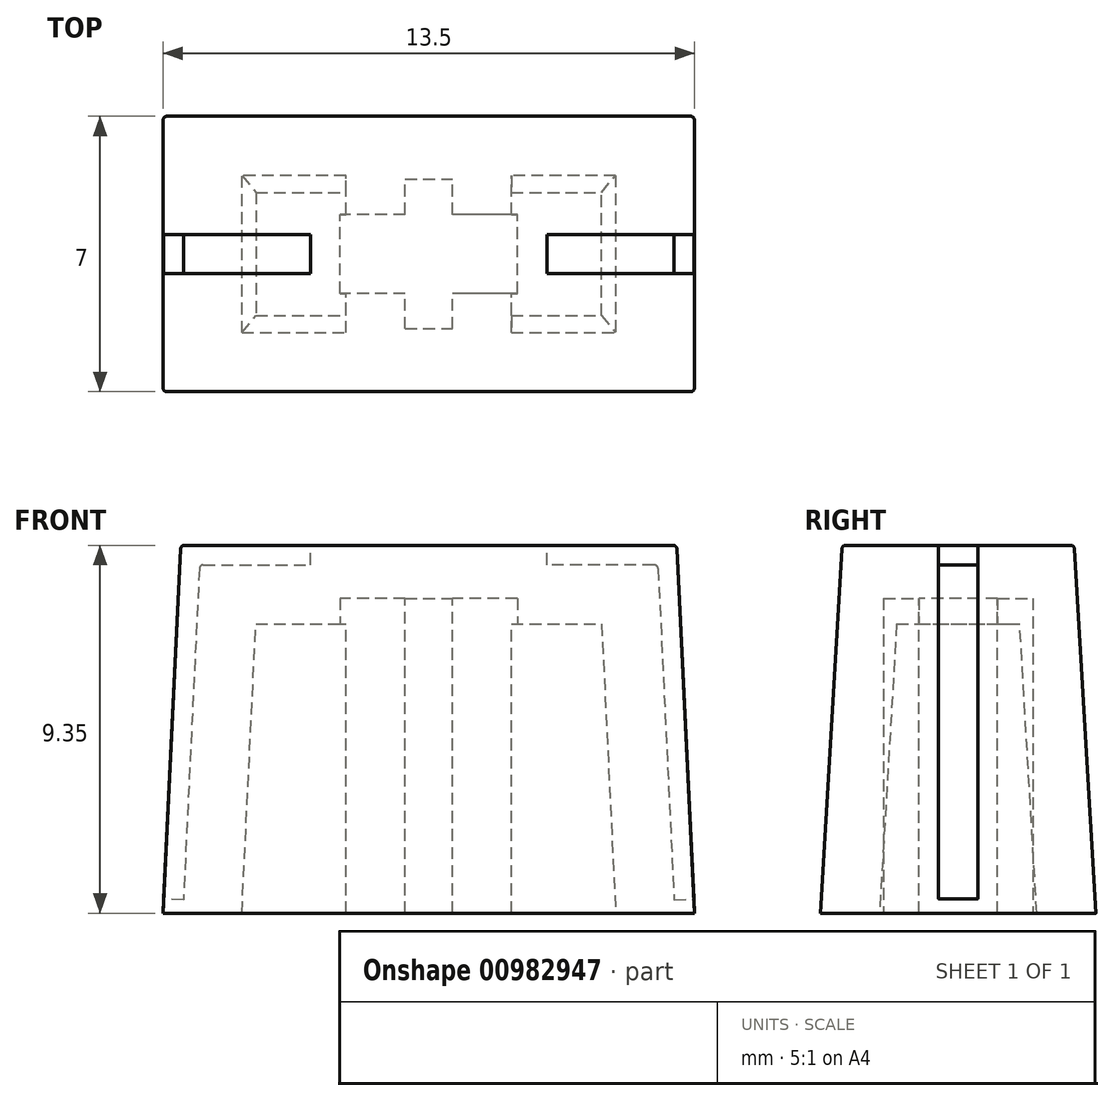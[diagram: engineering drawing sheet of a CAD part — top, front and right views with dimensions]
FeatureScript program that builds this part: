
annotation { "Feature Type Name" : "Feature", "Feature Type Description" : "" }
export const myFeature = defineFeature(function(context is Context, id is Id, definition is map)
    precondition{}
    {
        {
            var Q0;
            Q0=qCreatedBy(makeId("Top.planeOp"),FACE);
            var sketch = newSketch(context, id + "F0", { "sketchPlane" : qUnion([Q0])});
            skLineSegment(sketch, "E0.bottom", {"start": v(6.75, 3.5) * mm, "end": v(-6.75, 3.5) * mm});
            skLineSegment(sketch, "E0.top", {"start": v(6.75, -3.5) * mm, "end": v(-6.75, -3.5) * mm});
            skLineSegment(sketch, "E0.left", {"start": v(6.75, 3.5) * mm, "end": v(6.75, -3.5) * mm});
            skLineSegment(sketch, "E0.right", {"start": v(-6.75, 3.5) * mm, "end": v(-6.75, -3.5) * mm});
            skPoint(sketch, "E0.middle", {"position": v(0, 0) * mm});
            skSolve(sketch);
        }
        {
            var Q0;
            Q0=makeQuery(id+"F0.imprint","IMPRINT",FACE,{"disambiguationData":[TD([[makeQuery(id+"F0.imprint","IMPRINT",EDGE,{"derivedFrom":sQuery(id+"F0.wireOp",EDGE,"E0.bottom")}),1.0]])]});
            extrude(context, id + "F1", {"entities" : qUnion([Q0]), "depth" : 9.35 * mm, "offsetDistance" : 25 * mm});
        }
        {
            var Q0;
            Q0=makeQuery(id+"F1.opExtrude","CAP_EDGE",EDGE,{"disambiguationData":[OSD([sQuery(id+"F0.wireOp",EDGE,"E0.top")])],"isStart":false});
            var Q1;
            Q1=makeQuery(id+"F1.opExtrude","CAP_EDGE",EDGE,{"disambiguationData":[OSD([sQuery(id+"F0.wireOp",EDGE,"E0.bottom")])],"isStart":false});
            chamfer(context, id + "F2", {"entities" : qUnion([Q0, Q1]), "chamferType" : ChamferType.OFFSET_ANGLE, "width" : 9.35 * mm, "oppositeDirection" : false, "angle" : 3.37 * degree, "tangentPropagation" : true});
        }
        {
            var Q0;
            Q0=makeQuery(id+"F1.opExtrude","CAP_EDGE",EDGE,{"disambiguationData":[OSD([sQuery(id+"F0.wireOp",EDGE,"E0.right")])],"isStart":false});
            var Q1;
            Q1=makeQuery(id+"F1.opExtrude","CAP_EDGE",EDGE,{"disambiguationData":[OSD([sQuery(id+"F0.wireOp",EDGE,"E0.left")])],"isStart":false});
            chamfer(context, id + "F3", {"entities" : qUnion([Q0, Q1]), "chamferType" : ChamferType.OFFSET_ANGLE, "width" : 9.35 * mm, "oppositeDirection" : true, "angle" : 2.76 * degree, "tangentPropagation" : true});
        }
        {
            var Q0;
            Q0=makeQuery(id+"F1.opExtrude","CAP_FACE",FACE,{"disambiguationData":[OSD([sQuery(id+"F0.wireOp",EDGE,"E0.bottom"),sQuery(id+"F0.wireOp",EDGE,"E0.top"),sQuery(id+"F0.wireOp",EDGE,"E0.left"),sQuery(id+"F0.wireOp",EDGE,"E0.right")])],"isStart":true});
            var sketch = newSketch(context, id + "F4", { "sketchPlane" : qUnion([Q0])});
            skLineSegment(sketch, "E1.bottom", {"start": v(-0.6, 1.9) * mm, "end": v(0.6, 1.9) * mm});
            skLineSegment(sketch, "E1.top", {"start": v(-0.6, -1.9) * mm, "end": v(0.6, -1.9) * mm});
            skLineSegment(sketch, "E1.left", {"start": v(-0.6, 1.9) * mm, "end": v(-0.6, -1.9) * mm});
            skLineSegment(sketch, "E1.right", {"start": v(0.6, 1.9) * mm, "end": v(0.6, -1.9) * mm});
            skPoint(sketch, "E1.middle", {"position": v(0, 0) * mm});
            skSolve(sketch);
        }
        {
            var Q0;
            Q0=makeQuery(id+"F4.imprint","IMPRINT",FACE,{"disambiguationData":[TD([[makeQuery(id+"F4.imprint","IMPRINT",EDGE,{"derivedFrom":sQuery(id+"F4.wireOp",EDGE,"E1.bottom")}),-1.0]])]});
            extrude(context, id + "F5", {"entities" : qUnion([Q0]), "operationType" : NewBodyOperationType.REMOVE, "oppositeDirection" : true, "depth" : 8 * mm, "offsetDistance" : 25 * mm});
        }
        {
            var Q0;
            Q0=makeQuery(id+"F1.opExtrude","CAP_FACE",FACE,{"disambiguationData":[OSD([sQuery(id+"F0.wireOp",EDGE,"E0.bottom"),sQuery(id+"F0.wireOp",EDGE,"E0.top"),sQuery(id+"F0.wireOp",EDGE,"E0.left"),sQuery(id+"F0.wireOp",EDGE,"E0.right")])],"isStart":false});
            var sketch = newSketch(context, id + "F6", { "sketchPlane" : qUnion([Q0])});
            skLineSegment(sketch, "E2.bottom", {"start": v(-6.3, -0.5) * mm, "end": v(-3, -0.5) * mm});
            skLineSegment(sketch, "E2.top", {"start": v(-6.3, 0.5) * mm, "end": v(-3, 0.5) * mm});
            skLineSegment(sketch, "E2.left", {"start": v(-6.3, -0.5) * mm, "end": v(-6.3, 0.5) * mm});
            skLineSegment(sketch, "E2.right", {"start": v(-3, -0.5) * mm, "end": v(-3, 0.5) * mm});
            skLineSegment(sketch, "E3.MirrorCS", {"start": v(6.3, 0.5) * mm, "end": v(3, 0.5) * mm});
            skLineSegment(sketch, "E4.MirrorCS", {"start": v(6.3, -0.5) * mm, "end": v(3, -0.5) * mm});
            skLineSegment(sketch, "E5.MirrorCS", {"start": v(3, -0.5) * mm, "end": v(3, 0.5) * mm});
            skLineSegment(sketch, "E6.MirrorCS", {"start": v(6.3, -0.5) * mm, "end": v(6.3, 0.5) * mm});
            skSolve(sketch);
        }
        {
            var Q0;
            Q0=makeQuery(id+"F6.imprint","IMPRINT",FACE,{"disambiguationData":[TD([[makeQuery(id+"F6.imprint","IMPRINT",EDGE,{"derivedFrom":sQuery(id+"F6.wireOp",EDGE,"E2.bottom")}),1.0]])]});
            var Q1;
            Q1=makeQuery(id+"F6.imprint","IMPRINT",FACE,{"disambiguationData":[TD([[makeQuery(id+"F6.imprint","IMPRINT",EDGE,{"derivedFrom":sQuery(id+"F6.wireOp",EDGE,"E3.MirrorCS")}),1.0]])]});
            extrude(context, id + "F7", {"entities" : qUnion([Q0, Q1]), "operationType" : NewBodyOperationType.REMOVE, "oppositeDirection" : true, "depth" : 0.5 * mm, "offsetDistance" : 25 * mm});
        }
        {
            var Q0;
            Q0=makeQuery(id+"F3.opChamfer","BLEND_FACE",FACE,{"disambiguationData":[OSD([sQuery(id+"F0.wireOp",EDGE,"E0.right")])]});
            var sketch = newSketch(context, id + "F8", { "sketchPlane" : qUnion([Q0])});
            skLineSegment(sketch, "E7.bottom", {"start": v(-0.5, 9.04) * mm, "end": v(0.5, 9.04) * mm});
            skLineSegment(sketch, "E7.top", {"start": v(-0.5, 0.04) * mm, "end": v(0.5, 0.04) * mm});
            skLineSegment(sketch, "E7.left", {"start": v(-0.5, 9.04) * mm, "end": v(-0.5, 0.04) * mm});
            skLineSegment(sketch, "E7.right", {"start": v(0.5, 9.04) * mm, "end": v(0.5, 0.04) * mm});
            skSolve(sketch);
        }
        {
            var Q0;
            Q0=makeQuery(id+"F8.imprint","IMPRINT",FACE,{"disambiguationData":[TD([[makeQuery(id+"F8.imprint","IMPRINT",EDGE,{"derivedFrom":sQuery(id+"F8.wireOp",EDGE,"E7.bottom")}),-1.0]])]});
            extrude(context, id + "F9", {"entities" : qUnion([Q0]), "operationType" : NewBodyOperationType.REMOVE, "oppositeDirection" : true, "depth" : 0.5 * mm, "offsetDistance" : 25 * mm});
        }
        {
            var Q0;
            Q0=makeQuery(id+"F3.opChamfer","BLEND_FACE",FACE,{"disambiguationData":[OSD([sQuery(id+"F0.wireOp",EDGE,"E0.left")])]});
            var sketch = newSketch(context, id + "F10", { "sketchPlane" : qUnion([Q0])});
            skLineSegment(sketch, "E8.bottom", {"start": v(-0.5, 9.04) * mm, "end": v(0.5, 9.04) * mm});
            skLineSegment(sketch, "E8.top", {"start": v(-0.5, 0.04) * mm, "end": v(0.5, 0.04) * mm});
            skLineSegment(sketch, "E8.left", {"start": v(-0.5, 9.04) * mm, "end": v(-0.5, 0.04) * mm});
            skLineSegment(sketch, "E8.right", {"start": v(0.5, 9.04) * mm, "end": v(0.5, 0.04) * mm});
            skSolve(sketch);
        }
        {
            var Q0;
            Q0=makeQuery(id+"F10.imprint","IMPRINT",FACE,{"disambiguationData":[TD([[makeQuery(id+"F10.imprint","IMPRINT",EDGE,{"derivedFrom":sQuery(id+"F10.wireOp",EDGE,"E8.top")}),1.0]])]});
            extrude(context, id + "F11", {"entities" : qUnion([Q0]), "operationType" : NewBodyOperationType.REMOVE, "oppositeDirection" : true, "depth" : 0.5 * mm, "offsetDistance" : 25 * mm});
        }
        {
            var Q0;
            Q0=makeQuery(id+"F1.opExtrude","CAP_FACE",FACE,{"disambiguationData":[OSD([sQuery(id+"F0.wireOp",EDGE,"E0.bottom"),sQuery(id+"F0.wireOp",EDGE,"E0.top"),sQuery(id+"F0.wireOp",EDGE,"E0.left"),sQuery(id+"F0.wireOp",EDGE,"E0.right")])],"isStart":true});
            shell(context, id + "F12", {"entities" : qUnion([Q0]), "thickness" : 1.5 * mm});
        }
        {
            var Q0;
            Q0=makeQuery(id+"F1.opExtrude","CAP_FACE",FACE,{"disambiguationData":[OSD([sQuery(id+"F0.wireOp",EDGE,"E0.bottom"),sQuery(id+"F0.wireOp",EDGE,"E0.top"),sQuery(id+"F0.wireOp",EDGE,"E0.left"),sQuery(id+"F0.wireOp",EDGE,"E0.right")])],"isStart":true});
            var sketch = newSketch(context, id + "F13", { "sketchPlane" : qUnion([Q0])});
            skLineSegment(sketch, "E9.bottom", {"start": v(2.25, -1) * mm, "end": v(-2.25, -1) * mm});
            skLineSegment(sketch, "E9.top", {"start": v(2.25, 1) * mm, "end": v(-2.25, 1) * mm});
            skLineSegment(sketch, "E9.left", {"start": v(2.25, -1) * mm, "end": v(2.25, 1) * mm});
            skLineSegment(sketch, "E9.right", {"start": v(-2.25, -1) * mm, "end": v(-2.25, 1) * mm});
            skPoint(sketch, "E9.middle", {"position": v(0, 0) * mm});
            skSolve(sketch);
        }
        {
            var Q0;
            {var subQ0=sQuery(id+"F13.wireOp",EDGE,"E9.bottom");var subQ1=sQuery(id+"F4.wireOp",EDGE,"E1.left");var subQ2=makeQuery(id+"F5.boolean.opBoolean","COPY",EDGE,{"derivedFrom":makeQuery(id+"F5.opExtrude","CAP_EDGE",EDGE,{"disambiguationData":[OSD([subQ1])],"isStart":true})});var subQ3=makeQuery(id+"F13.imprint","INTERSECT",VERTEX,{"derivedFrom":[subQ2,subQ0]});Q0=makeQuery(id+"F13.imprint","IMPRINT",FACE,{"disambiguationData":[TD([[makeQuery(id+"F13.imprint","IMPRINT",EDGE,{"disambiguationData":[TD([[subQ3,-1.0]])],"derivedFrom":subQ0}),-1.0]])]});}
            var Q1;
            {var subQ0=sQuery(id+"F13.wireOp",EDGE,"E9.bottom");var subQ1=sQuery(id+"F4.wireOp",EDGE,"E1.right");var subQ2=makeQuery(id+"F12.opShell","OFFSET_EDGE",EDGE,{"disambiguationData":[OSD([subQ1])]});var subQ3=makeQuery(id+"F13.imprint","INTERSECT",VERTEX,{"derivedFrom":[subQ2,subQ0]});Q1=makeQuery(id+"F13.imprint","IMPRINT",FACE,{"disambiguationData":[TD([[makeQuery(id+"F13.imprint","IMPRINT",EDGE,{"disambiguationData":[TD([[subQ3,-1.0]])],"derivedFrom":subQ0}),-1.0]])]});}
            extrude(context, id + "F14", {"entities" : qUnion([Q0, Q1]), "operationType" : NewBodyOperationType.REMOVE, "oppositeDirection" : true, "depth" : 8 * mm, "offsetDistance" : 25 * mm});
        }
        {
            var Q0;
            Q0=makeQuery(id+"F3.opChamfer","BLEND_EDGE",EDGE,{"blendedFrom":[makeQuery(id+"F1.opExtrude","CAP_EDGE",EDGE,{"disambiguationData":[OSD([sQuery(id+"F0.wireOp",EDGE,"E0.left")])],"isStart":false}),makeQuery(id+"F2.opChamfer","BLEND_FACE",FACE,{"disambiguationData":[OSD([sQuery(id+"F0.wireOp",EDGE,"E0.top")])]})],"blendedInto":[makeQuery(id+"F2.opChamfer","BLEND_FACE",FACE,{"disambiguationData":[OSD([sQuery(id+"F0.wireOp",EDGE,"E0.top")])]})]});
            var Q1;
            Q1=makeQuery(id+"F3.opChamfer","BLEND_EDGE",EDGE,{"blendedFrom":[makeQuery(id+"F1.opExtrude","CAP_EDGE",EDGE,{"disambiguationData":[OSD([sQuery(id+"F0.wireOp",EDGE,"E0.left")])],"isStart":false}),makeQuery(id+"F2.opChamfer","BLEND_FACE",FACE,{"disambiguationData":[OSD([sQuery(id+"F0.wireOp",EDGE,"E0.bottom")])]})],"blendedInto":[makeQuery(id+"F2.opChamfer","BLEND_FACE",FACE,{"disambiguationData":[OSD([sQuery(id+"F0.wireOp",EDGE,"E0.bottom")])]})]});
            var Q2;
            {var subQ0=sQuery(id+"F0.wireOp",EDGE,"E0.bottom");var subQ1=sQuery(id+"F0.wireOp",EDGE,"E0.left");var subQ2=makeQuery(id+"F1.opExtrude","CAP_FACE",FACE,{"disambiguationData":[OSD([subQ0,sQuery(id+"F0.wireOp",EDGE,"E0.top"),subQ1,sQuery(id+"F0.wireOp",EDGE,"E0.right")])],"isStart":false});Q2=makeQuery(id+"F7.boolean.opBoolean","SPLIT",EDGE,{"disambiguationData":[TD([makeQuery(id+"F2.opChamfer","BLEND_FACE",FACE,{"disambiguationData":[OSD([subQ0])]})])],"derivedFrom":makeQuery(id+"F3.opChamfer","BLEND_EDGE",EDGE,{"blendedFrom":[makeQuery(id+"F1.opExtrude","CAP_EDGE",EDGE,{"disambiguationData":[OSD([subQ1])],"isStart":false}),subQ2],"blendedInto":[subQ2]})});}
            var Q3;
            {var subQ0=sQuery(id+"F0.wireOp",EDGE,"E0.left");var subQ1=sQuery(id+"F0.wireOp",EDGE,"E0.top");var subQ2=makeQuery(id+"F1.opExtrude","CAP_FACE",FACE,{"disambiguationData":[OSD([sQuery(id+"F0.wireOp",EDGE,"E0.bottom"),subQ1,subQ0,sQuery(id+"F0.wireOp",EDGE,"E0.right")])],"isStart":false});Q3=makeQuery(id+"F7.boolean.opBoolean","SPLIT",EDGE,{"disambiguationData":[TD([makeQuery(id+"F2.opChamfer","BLEND_FACE",FACE,{"disambiguationData":[OSD([subQ1])]})])],"derivedFrom":makeQuery(id+"F3.opChamfer","BLEND_EDGE",EDGE,{"blendedFrom":[makeQuery(id+"F1.opExtrude","CAP_EDGE",EDGE,{"disambiguationData":[OSD([subQ0])],"isStart":false}),subQ2],"blendedInto":[subQ2]})});}
            var Q4;
            {var subQ0=sQuery(id+"F0.wireOp",EDGE,"E0.top");Q4=makeQuery(id+"F2.opChamfer","BLEND_EDGE",EDGE,{"blendedFrom":[makeQuery(id+"F1.opExtrude","CAP_EDGE",EDGE,{"disambiguationData":[OSD([subQ0])],"isStart":false}),makeQuery(id+"F1.opExtrude","CAP_FACE",FACE,{"disambiguationData":[OSD([sQuery(id+"F0.wireOp",EDGE,"E0.bottom"),subQ0,sQuery(id+"F0.wireOp",EDGE,"E0.left"),sQuery(id+"F0.wireOp",EDGE,"E0.right")])],"isStart":false})],"blendedInto":[makeQuery(id+"F1.opExtrude","CAP_FACE",FACE,{"disambiguationData":[OSD([sQuery(id+"F0.wireOp",EDGE,"E0.bottom"),subQ0,sQuery(id+"F0.wireOp",EDGE,"E0.left"),sQuery(id+"F0.wireOp",EDGE,"E0.right")])],"isStart":false})]});}
            var Q5;
            {var subQ0=sQuery(id+"F0.wireOp",EDGE,"E0.bottom");Q5=makeQuery(id+"F2.opChamfer","BLEND_EDGE",EDGE,{"blendedFrom":[makeQuery(id+"F1.opExtrude","CAP_EDGE",EDGE,{"disambiguationData":[OSD([subQ0])],"isStart":false}),makeQuery(id+"F1.opExtrude","CAP_FACE",FACE,{"disambiguationData":[OSD([subQ0,sQuery(id+"F0.wireOp",EDGE,"E0.top"),sQuery(id+"F0.wireOp",EDGE,"E0.left"),sQuery(id+"F0.wireOp",EDGE,"E0.right")])],"isStart":false})],"blendedInto":[makeQuery(id+"F1.opExtrude","CAP_FACE",FACE,{"disambiguationData":[OSD([subQ0,sQuery(id+"F0.wireOp",EDGE,"E0.top"),sQuery(id+"F0.wireOp",EDGE,"E0.left"),sQuery(id+"F0.wireOp",EDGE,"E0.right")])],"isStart":false})]});}
            var Q6;
            Q6=makeQuery(id+"F3.opChamfer","BLEND_EDGE",EDGE,{"blendedFrom":[makeQuery(id+"F1.opExtrude","CAP_EDGE",EDGE,{"disambiguationData":[OSD([sQuery(id+"F0.wireOp",EDGE,"E0.right")])],"isStart":false}),makeQuery(id+"F2.opChamfer","BLEND_FACE",FACE,{"disambiguationData":[OSD([sQuery(id+"F0.wireOp",EDGE,"E0.bottom")])]})],"blendedInto":[makeQuery(id+"F2.opChamfer","BLEND_FACE",FACE,{"disambiguationData":[OSD([sQuery(id+"F0.wireOp",EDGE,"E0.bottom")])]})]});
            var Q7;
            Q7=makeQuery(id+"F3.opChamfer","BLEND_EDGE",EDGE,{"blendedFrom":[makeQuery(id+"F1.opExtrude","CAP_EDGE",EDGE,{"disambiguationData":[OSD([sQuery(id+"F0.wireOp",EDGE,"E0.right")])],"isStart":false}),makeQuery(id+"F2.opChamfer","BLEND_FACE",FACE,{"disambiguationData":[OSD([sQuery(id+"F0.wireOp",EDGE,"E0.top")])]})],"blendedInto":[makeQuery(id+"F2.opChamfer","BLEND_FACE",FACE,{"disambiguationData":[OSD([sQuery(id+"F0.wireOp",EDGE,"E0.top")])]})]});
            var Q8;
            {var subQ0=sQuery(id+"F0.wireOp",EDGE,"E0.right");var subQ1=sQuery(id+"F0.wireOp",EDGE,"E0.top");var subQ2=makeQuery(id+"F1.opExtrude","CAP_FACE",FACE,{"disambiguationData":[OSD([sQuery(id+"F0.wireOp",EDGE,"E0.bottom"),subQ1,sQuery(id+"F0.wireOp",EDGE,"E0.left"),subQ0])],"isStart":false});Q8=makeQuery(id+"F7.boolean.opBoolean","SPLIT",EDGE,{"disambiguationData":[TD([makeQuery(id+"F2.opChamfer","BLEND_FACE",FACE,{"disambiguationData":[OSD([subQ1])]})])],"derivedFrom":makeQuery(id+"F3.opChamfer","BLEND_EDGE",EDGE,{"blendedFrom":[makeQuery(id+"F1.opExtrude","CAP_EDGE",EDGE,{"disambiguationData":[OSD([subQ0])],"isStart":false}),subQ2],"blendedInto":[subQ2]})});}
            var Q9;
            {var subQ0=sQuery(id+"F0.wireOp",EDGE,"E0.right");var subQ1=sQuery(id+"F0.wireOp",EDGE,"E0.bottom");var subQ2=makeQuery(id+"F1.opExtrude","CAP_FACE",FACE,{"disambiguationData":[OSD([subQ1,sQuery(id+"F0.wireOp",EDGE,"E0.top"),sQuery(id+"F0.wireOp",EDGE,"E0.left"),subQ0])],"isStart":false});Q9=makeQuery(id+"F7.boolean.opBoolean","SPLIT",EDGE,{"disambiguationData":[TD([makeQuery(id+"F2.opChamfer","BLEND_FACE",FACE,{"disambiguationData":[OSD([subQ1])]})])],"derivedFrom":makeQuery(id+"F3.opChamfer","BLEND_EDGE",EDGE,{"blendedFrom":[makeQuery(id+"F1.opExtrude","CAP_EDGE",EDGE,{"disambiguationData":[OSD([subQ0])],"isStart":false}),subQ2],"blendedInto":[subQ2]})});}
            var Q10;
            Q10=makeQuery(id+"F9.boolean.opBoolean","INTERSECT",EDGE,{"derivedFrom":[makeQuery(id+"F7.boolean.opBoolean","COPY",FACE,{"derivedFrom":makeQuery(id+"F7.opExtrude","CAP_FACE",FACE,{"disambiguationData":[OSD([sQuery(id+"F6.wireOp",EDGE,"E2.bottom"),sQuery(id+"F6.wireOp",EDGE,"E2.top"),sQuery(id+"F6.wireOp",EDGE,"E2.left"),sQuery(id+"F6.wireOp",EDGE,"E2.right")])],"isStart":false})}),makeQuery(id+"F9.opExtrude","CAP_FACE",FACE,{"disambiguationData":[OSD([sQuery(id+"F8.wireOp",EDGE,"E7.bottom"),sQuery(id+"F8.wireOp",EDGE,"E7.top"),sQuery(id+"F8.wireOp",EDGE,"E7.left"),sQuery(id+"F8.wireOp",EDGE,"E7.right")])],"isStart":false})]});
            var Q11;
            Q11=makeQuery(id+"F11.boolean.opBoolean","INTERSECT",EDGE,{"derivedFrom":[makeQuery(id+"F7.boolean.opBoolean","COPY",FACE,{"derivedFrom":makeQuery(id+"F7.opExtrude","CAP_FACE",FACE,{"disambiguationData":[OSD([sQuery(id+"F6.wireOp",EDGE,"E3.MirrorCS"),sQuery(id+"F6.wireOp",EDGE,"E4.MirrorCS"),sQuery(id+"F6.wireOp",EDGE,"E5.MirrorCS"),sQuery(id+"F6.wireOp",EDGE,"E6.MirrorCS")])],"isStart":false})}),makeQuery(id+"F11.opExtrude","CAP_FACE",FACE,{"disambiguationData":[OSD([sQuery(id+"F10.wireOp",EDGE,"E8.bottom"),sQuery(id+"F10.wireOp",EDGE,"E8.top"),sQuery(id+"F10.wireOp",EDGE,"E8.left"),sQuery(id+"F10.wireOp",EDGE,"E8.right")])],"isStart":false})]});
            fillet(context, id + "F15", {"entities" : qUnion([Q0, Q1, Q2, Q3, Q4, Q5, Q6, Q7, Q8, Q9, Q10, Q11]), "radius" : .1 * mm, "tangentPropagation" : true, "allowEdgeOverflow" : false});
        }
    });
